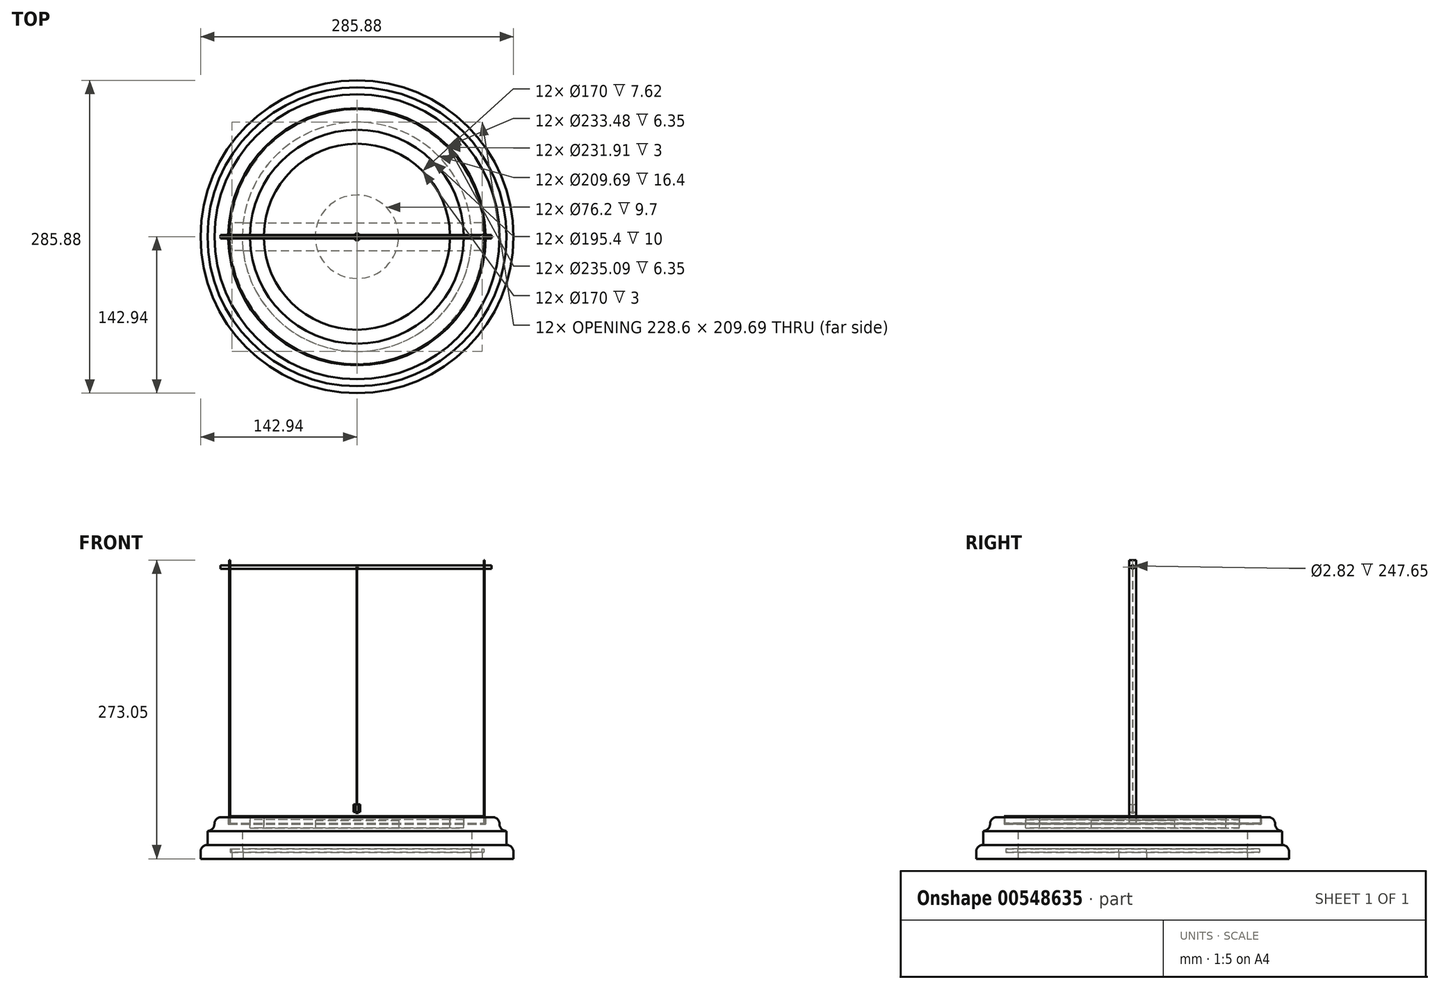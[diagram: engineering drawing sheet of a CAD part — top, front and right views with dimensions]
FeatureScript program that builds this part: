
annotation { "Feature Type Name" : "Feature", "Feature Type Description" : "" }
export const myFeature = defineFeature(function(context is Context, id is Id, definition is map)
    precondition{}
    {
        {
            var Q0;
            Q0=qCreatedBy(makeId("Front.planeOp"),FACE);
            var sketch = newSketch(context, id + "F0", { "sketchPlane" : qUnion([Q0])});
            skLineSegment(sketch, "E0", {"start": v(0, 38.1) * mm, "end": v(-85, 38.1) * mm});
            skLineSegment(sketch, "E1", {"start": v(-85, 38.1) * mm, "end": v(-85, 28.1) * mm});
            skLineSegment(sketch, "E2", {"start": v(-97.7, 28.1) * mm, "end": v(-97.7, 38.1) * mm});
            skLineSegment(sketch, "E3", {"start": v(-97.7, 38.1) * mm, "end": v(-116.75, 38.1) * mm});
            skLineSegment(sketch, "E4", {"start": v(-142.94, 0) * mm, "end": v(-104.84, 0) * mm});
            skLineSegment(sketch, "E5", {"start": v(-104.84, 25.4) * mm, "end": v(-104.84, 9) * mm});
            skLineSegment(sketch, "E6", {"start": v(-104.84, 9) * mm, "end": v(-115.96, 9) * mm});
            skLineSegment(sketch, "E7", {"start": v(-115.96, 9) * mm, "end": v(-115.96, 6) * mm});
            skLineSegment(sketch, "E8", {"start": v(-115.96, 6) * mm, "end": v(-104.84, 6) * mm});
            skLineSegment(sketch, "E9", {"start": v(-104.84, 6) * mm, "end": v(-104.84, 0) * mm});
            skLineSegment(sketch, "E10", {"start": v(-136.6, 12.7) * mm, "end": v(-136.6, 25.4) * mm});
            skArc(sketch, "E11", {"start": v(-136.6, 25.4) * mm, "mid": v(-132.1, 27.26) * mm, "end": v(-130.24, 31.75) * mm});
            skLineSegment(sketch, "E12", {"start": v(-117.54, 38.1) * mm, "end": v(-117.54, 31.75) * mm});
            skLineSegment(sketch, "E13", {"start": v(-117.54, 31.75) * mm, "end": v(-116.75, 31.75) * mm});
            skLineSegment(sketch, "E14", {"start": v(-116.75, 31.75) * mm, "end": v(-116.75, 38.1) * mm});
            skLineSegment(sketch, "E15", {"start": v(-97.7, 28.1) * mm, "end": v(-85, 28.1) * mm});
            skLineSegment(sketch, "E16", {"start": v(-117.54, 38.1) * mm, "end": v(-123.9, 38.1) * mm});
            skArc(sketch, "E17", {"start": v(-123.9, 38.1) * mm, "mid": v(-128.38, 36.24) * mm, "end": v(-130.24, 31.75) * mm});
            skLineSegment(sketch, "E18", {"start": v(-136.6, 31.75) * mm, "end": v(-130.24, 31.75) * mm, "construction": true});
            skLineSegment(sketch, "E19", {"start": v(-123.9, 31.75) * mm, "end": v(-130.24, 31.75) * mm, "construction": true});
            skLineSegment(sketch, "E20", {"start": v(-136.6, 31.75) * mm, "end": v(-136.6, 25.4) * mm, "construction": true});
            skLineSegment(sketch, "E21", {"start": v(-123.9, 38.1) * mm, "end": v(-123.9, 31.75) * mm, "construction": true});
            skArc(sketch, "E22", {"start": v(-136.6, 12.7) * mm, "mid": v(-141.08, 10.84) * mm, "end": v(-142.94, 6.35) * mm});
            skLineSegment(sketch, "E23", {"start": v(-136.6, 12.7) * mm, "end": v(-136.6, 6.35) * mm, "construction": true});
            skLineSegment(sketch, "E24", {"start": v(-136.6, 6.35) * mm, "end": v(-142.94, 6.35) * mm, "construction": true});
            skLineSegment(sketch, "E25", {"start": v(-142.94, 6.35) * mm, "end": v(-142.94, 0) * mm});
            skLineSegment(sketch, "E26", {"start": v(-104.84, 25.4) * mm, "end": v(-38.1, 25.4) * mm});
            skLineSegment(sketch, "E27", {"start": v(-38.1, 25.4) * mm, "end": v(-38.1, 35.1) * mm});
            skLineSegment(sketch, "E28", {"start": v(-38.1, 35.1) * mm, "end": v(0, 35.1) * mm});
            skLineSegment(sketch, "E29", {"start": v(0, 35.1) * mm, "end": v(0, 38.1) * mm});
            skSolve(sketch);
        }
        {
            var Q0;
            Q0=makeQuery(id+"F0.imprint","IMPRINT",FACE,{"disambiguationData":[TD([[makeQuery(id+"F0.imprint","IMPRINT",EDGE,{"derivedFrom":sQuery(id+"F0.wireOp",EDGE,"E0")}),1.0]])]});
            var Q1;
            Q1=sQuery(id+"F0.wireOp",EDGE,"E29");
            revolve(context, id + "F1", {"entities" : qUnion([Q0]), "axis" : qUnion([Q1]), "revolveType" : RevolveType.FULL});
        }
        {
            var Q0;
            Q0=makeQuery(id+"F1.opRevolve","SWEPT_FACE",FACE,{"disambiguationData":[OSD([sQuery(id+"F0.wireOp",EDGE,"E4")])]});
            var sketch = newSketch(context, id + "F2", { "sketchPlane" : qUnion([Q0])});
            skLineSegment(sketch, "E30.bottom", {"start": v(-114.3, 12.7) * mm, "end": v(114.3, 12.7) * mm});
            skLineSegment(sketch, "E30.top", {"start": v(-114.3, -12.7) * mm, "end": v(114.3, -12.7) * mm});
            skLineSegment(sketch, "E30.left", {"start": v(-114.3, 12.7) * mm, "end": v(-114.3, -12.7) * mm});
            skLineSegment(sketch, "E30.right", {"start": v(114.3, 12.7) * mm, "end": v(114.3, -12.7) * mm});
            skPoint(sketch, "E30.middle", {"position": v(0, 0) * mm});
            skSolve(sketch);
        }
        {
            var Q0;
            Q0 = qSketchRegion(id + "F2", true);
            var Q1;
            Q1=makeQuery(id+"F1.opRevolve","SWEPT_FACE",FACE,{"disambiguationData":[OSD([sQuery(id+"F0.wireOp",EDGE,"E6")])]});
            extrude(context, id + "F3", {"entities" : qUnion([Q0]), "operationType" : NewBodyOperationType.REMOVE, "endBound" : BoundingType.UP_TO_SURFACE, "oppositeDirection" : true, "depth" : 25.4 * mm, "endBoundEntityFace" : qUnion([Q1]), "offsetDistance" : 25.4 * mm});
        }
        {
            var Q0;
            Q0=makeQuery(id+"F1.opRevolve","SWEPT_FACE",FACE,{"disambiguationData":[OSD([sQuery(id+"F0.wireOp",EDGE,"E3")])]});
            var sketch = newSketch(context, id + "F4", { "sketchPlane" : qUnion([Q0])});
            skLineSegment(sketch, "E31.bottom", {"start": v(-116.62, 3.17) * mm, "end": v(-115.82, 3.17) * mm});
            skLineSegment(sketch, "E31.top", {"start": v(-116.62, -3.18) * mm, "end": v(-115.82, -3.18) * mm});
            skLineSegment(sketch, "E31.left", {"start": v(-116.62, 3.17) * mm, "end": v(-116.62, -3.17) * mm});
            skLineSegment(sketch, "E31.right", {"start": v(-115.82, 3.17) * mm, "end": v(-115.82, -3.18) * mm});
            skLineSegment(sketch, "E32", {"start": v(-115.82, 0) * mm, "end": v(0, 0) * mm, "construction": true});
            skLineSegment(sketch, "E33.bottom", {"start": v(115.82, 3.18) * mm, "end": v(116.62, 3.18) * mm});
            skLineSegment(sketch, "E33.top", {"start": v(115.82, -3.17) * mm, "end": v(116.62, -3.17) * mm});
            skLineSegment(sketch, "E33.left", {"start": v(115.82, 3.18) * mm, "end": v(115.82, -3.17) * mm});
            skLineSegment(sketch, "E33.right", {"start": v(116.62, 3.17) * mm, "end": v(116.62, -3.18) * mm});
            skLineSegment(sketch, "E34", {"start": v(115.82, 0) * mm, "end": v(0, 0) * mm, "construction": true});
            skSolve(sketch);
        }
        {
            var Q0;
            Q0=makeQuery(id+"F4.imprint","IMPRINT",FACE,{"disambiguationData":[TD([[makeQuery(id+"F4.imprint","IMPRINT",EDGE,{"derivedFrom":sQuery(id+"F4.wireOp",EDGE,"E31.bottom")}),-1.0]])]});
            var Q1;
            Q1=makeQuery(id+"F4.imprint","IMPRINT",FACE,{"disambiguationData":[TD([[makeQuery(id+"F4.imprint","IMPRINT",EDGE,{"derivedFrom":sQuery(id+"F4.wireOp",EDGE,"E33.bottom")}),-1.0]])]});
            extrude(context, id + "F5", {"entities" : qUnion([Q0, Q1]), "operationType" : NewBodyOperationType.REMOVE, "oppositeDirection" : true, "depth" : 6.35 * mm, "offsetDistance" : 25.4 * mm});
        }
        {
            var Q0;
            Q0=qCreatedBy(makeId("Front.planeOp"),FACE);
            var sketch = newSketch(context, id + "F6", { "sketchPlane" : qUnion([Q0])});
            skLineSegment(sketch, "E35", {"start": v(-85, 35.71) * mm, "end": v(-85, 28.1) * mm});
            skLineSegment(sketch, "E36", {"start": v(-85, 28.1) * mm, "end": v(-97.7, 28.1) * mm});
            skLineSegment(sketch, "E37", {"start": v(-97.7, 28.1) * mm, "end": v(-97.7, 35.71) * mm});
            skLineSegment(sketch, "E38", {"start": v(-97.7, 35.71) * mm, "end": v(-85, 35.71) * mm});
            skLineSegment(sketch, "E39", {"start": v(0, 35.71) * mm, "end": v(0, 28.1) * mm, "construction": true});
            skLineSegment(sketch, "E40", {"start": v(0, 28.1) * mm, "end": v(0, 0) * mm, "construction": true});
            skSolve(sketch);
        }
        {
            var Q0;
            Q0 = qSketchRegion(id + "F6", true);
            var Q1;
            Q1=sQuery(id+"F6.wireOp",EDGE,"E39");
            revolve(context, id + "F7", {"entities" : qUnion([Q0]), "axis" : qUnion([Q1]), "revolveType" : RevolveType.FULL});
        }
        {
            var Q0;
            Q0=qCreatedBy(makeId("Front.planeOp"),FACE);
            var sketch = newSketch(context, id + "F8", { "sketchPlane" : qUnion([Q0])});
            skLineSegment(sketch, "E41", {"start": v(0, 35.71) * mm, "end": v(0, 38.71) * mm});
            skLineSegment(sketch, "E42", {"start": v(0, 35.71) * mm, "end": v(0, 0) * mm, "construction": true});
            skLineSegment(sketch, "E43", {"start": v(-97.7, 38.71) * mm, "end": v(-85, 38.71) * mm});
            skLineSegment(sketch, "E44", {"start": v(-85, 38.71) * mm, "end": v(-85, 35.71) * mm});
            skLineSegment(sketch, "E45", {"start": v(-85, 35.71) * mm, "end": v(-97.7, 35.71) * mm});
            skLineSegment(sketch, "E46", {"start": v(-97.7, 35.71) * mm, "end": v(-97.7, 38.71) * mm});
            skLineSegment(sketch, "E47", {"start": v(-85, 35.71) * mm, "end": v(0, 35.71) * mm, "construction": true});
            skSolve(sketch);
        }
        {
            var Q0;
            Q0 = qSketchRegion(id + "F8", true);
            var Q1;
            Q1=sQuery(id+"F8.wireOp",EDGE,"E41");
            revolve(context, id + "F9", {"entities" : qUnion([Q0]), "axis" : qUnion([Q1]), "revolveType" : RevolveType.FULL});
        }
        {
            var Q0;
            Q0=qCreatedBy(makeId("Front.planeOp"),FACE);
            var sketch = newSketch(context, id + "F10", { "sketchPlane" : qUnion([Q0])});
            skLineSegment(sketch, "E48", {"start": v(0, 0) * mm, "end": v(0, 32.54) * mm, "construction": true});
            skLineSegment(sketch, "E49", {"start": v(0, 32.54) * mm, "end": v(-116.74, 32.54) * mm, "construction": true});
            skLineSegment(sketch, "E50", {"start": v(-116.74, 32.54) * mm, "end": v(-116.74, 38.9) * mm});
            skLineSegment(sketch, "E51", {"start": v(-116.74, 38.9) * mm, "end": v(-117.53, 38.9) * mm});
            skLineSegment(sketch, "E52", {"start": v(-117.53, 38.9) * mm, "end": v(-117.53, 32.54) * mm});
            skLineSegment(sketch, "E53", {"start": v(-117.53, 32.54) * mm, "end": v(-116.74, 32.54) * mm});
            skSolve(sketch);
        }
        {
            var Q0;
            Q0 = qSketchRegion(id + "F10", true);
            var Q1;
            Q1=sQuery(id+"F10.wireOp",EDGE,"E48");
            revolve(context, id + "F11", {"entities" : qUnion([Q0]), "axis" : qUnion([Q1]), "revolveType" : RevolveType.FULL});
        }
        {
            var Q0;
            Q0=makeQuery(id+"F1.opRevolve","SWEPT_FACE",FACE,{"disambiguationData":[OSD([sQuery(id+"F0.wireOp",EDGE,"E6")])]});
            var sketch = newSketch(context, id + "F12", { "sketchPlane" : qUnion([Q0])});
            skArc(sketch, "E54.0", {"start": v(104.07, 12.7) * mm, "mid": v(0, 104.84) * mm, "end": v(-104.07, 12.7) * mm});
            skArc(sketch, "E55.0", {"start": v(-104.07, -12.7) * mm, "mid": v(0, -104.84) * mm, "end": v(104.07, -12.7) * mm});
            skLineSegment(sketch, "E56.0", {"start": v(104.07, 12.7) * mm, "end": v(114.3, 12.7) * mm});
            skLineSegment(sketch, "E56.1", {"start": v(114.3, 12.7) * mm, "end": v(114.3, -12.7) * mm});
            skLineSegment(sketch, "E56.2", {"start": v(104.07, -12.7) * mm, "end": v(114.3, -12.7) * mm});
            skLineSegment(sketch, "E57.0", {"start": v(-114.3, 12.7) * mm, "end": v(-104.07, 12.7) * mm});
            skLineSegment(sketch, "E57.1", {"start": v(-114.3, 12.7) * mm, "end": v(-114.3, -12.7) * mm});
            skLineSegment(sketch, "E57.2", {"start": v(-114.3, -12.7) * mm, "end": v(-104.07, -12.7) * mm});
            skSolve(sketch);
        }
        {
            var Q0;
            {var subQ0=sQuery(id+"F12.wireOp",EDGE,"E56.0");Q0=makeQuery(id+"F12.imprint","IMPRINT",FACE,{"disambiguationData":[TD([[makeQuery(id+"F12.imprint","IMPRINT",EDGE,{"derivedFrom":subQ0}),-1.0]])]});}
            var Q1;
            {var subQ0=sQuery(id+"F12.wireOp",EDGE,"E57.0");Q1=makeQuery(id+"F12.imprint","IMPRINT",FACE,{"disambiguationData":[TD([[makeQuery(id+"F12.imprint","IMPRINT",EDGE,{"derivedFrom":subQ0}),-1.0]])]});}
            var Q2;
            {var subQ0=sQuery(id+"F12.wireOp",EDGE,"E54.0");Q2=makeQuery(id+"F12.imprint","IMPRINT",FACE,{"disambiguationData":[TD([[makeQuery(id+"F12.imprint","IMPRINT",EDGE,{"derivedFrom":subQ0}),1.0]])]});}
            extrude(context, id + "F13", {"entities" : qUnion([Q0, Q1, Q2]), "depth" : 3 * mm, "offsetDistance" : 25.4 * mm});
        }
        {
            var Q0;
            Q0=makeQuery(id+"F5.boolean.opBoolean","COPY",FACE,{"derivedFrom":makeQuery(id+"F5.opExtrude","CAP_FACE",FACE,{"disambiguationData":[OSD([sQuery(id+"F4.wireOp",EDGE,"E31.bottom"),sQuery(id+"F4.wireOp",EDGE,"E31.top"),sQuery(id+"F4.wireOp",EDGE,"E31.left"),sQuery(id+"F4.wireOp",EDGE,"E31.right")])],"isStart":false})});
            var sketch = newSketch(context, id + "F14", { "sketchPlane" : qUnion([Q0])});
            skLineSegment(sketch, "E58.bottom", {"start": v(-115.82, 3.17) * mm, "end": v(-116.62, 3.17) * mm});
            skLineSegment(sketch, "E58.top", {"start": v(-115.82, -3.17) * mm, "end": v(-116.62, -3.17) * mm});
            skLineSegment(sketch, "E58.left", {"start": v(-115.82, 3.17) * mm, "end": v(-115.82, -3.17) * mm});
            skLineSegment(sketch, "E58.right", {"start": v(-116.62, 3.17) * mm, "end": v(-116.62, -3.17) * mm});
            skLineSegment(sketch, "E59.bottom", {"start": v(115.82, 3.18) * mm, "end": v(116.61, 3.18) * mm});
            skLineSegment(sketch, "E59.top", {"start": v(115.82, -3.17) * mm, "end": v(116.61, -3.17) * mm});
            skLineSegment(sketch, "E59.left", {"start": v(115.82, 3.18) * mm, "end": v(115.82, -3.17) * mm});
            skLineSegment(sketch, "E59.right", {"start": v(116.61, 3.18) * mm, "end": v(116.61, -3.17) * mm});
            skSolve(sketch);
        }
        {
            var Q0;
            Q0=makeQuery(id+"F14.imprint","IMPRINT",FACE,{"disambiguationData":[TD([[makeQuery(id+"F14.imprint","IMPRINT",EDGE,{"derivedFrom":sQuery(id+"F14.wireOp",EDGE,"E59.bottom")}),-1.0]])]});
            var Q1;
            Q1=makeQuery(id+"F14.imprint","IMPRINT",FACE,{"disambiguationData":[TD([[makeQuery(id+"F14.imprint","IMPRINT",EDGE,{"derivedFrom":sQuery(id+"F14.wireOp",EDGE,"E58.bottom")}),-1.0]])]});
            extrude(context, id + "F15", {"entities" : qUnion([Q0, Q1]), "depth" : 241.3 * mm, "offsetDistance" : 25.4 * mm});
        }
        {
            var Q0;
            Q0=makeQuery(id+"F15.opExtrude","SWEPT_FACE",FACE,{"disambiguationData":[OSD([sQuery(id+"F14.wireOp",EDGE,"E59.right")])]});
            var sketch = newSketch(context, id + "F16", { "sketchPlane" : qUnion([Q0])});
            skCircle(sketch, "E60", {"center": v(0, 266.7) * mm, "radius": 1.59 * mm});
            skLineSegment(sketch, "E61", {"start": v(0, 266.7) * mm, "end": v(0, 273.05) * mm, "construction": true});
            skSolve(sketch);
        }
        {
            var Q0;
            Q0 = qSketchRegion(id + "F16", true);
            extrude(context, id + "F17", {"entities" : qUnion([Q0]), "operationType" : NewBodyOperationType.REMOVE, "endBound" : BoundingType.THROUGH_ALL, "oppositeDirection" : true, "depth" : 25.4 * mm, "offsetDistance" : 25.4 * mm});
        }
        {
            var Q0;
            Q0=makeQuery(id+"F15.opExtrude","SWEPT_FACE",FACE,{"disambiguationData":[OSD([sQuery(id+"F14.wireOp",EDGE,"E59.right")])]});
            var sketch = newSketch(context, id + "F18", { "sketchPlane" : qUnion([Q0])});
            skCircle(sketch, "E62", {"center": v(0, 266.7) * mm, "radius": 1.59 * mm});
            skCircle(sketch, "E63", {"center": v(0, 266.7) * mm, "radius": 1.4 * mm});
            skSolve(sketch);
        }
        {
            var Q0;
            Q0=makeQuery(id+"F18.imprint","IMPRINT",FACE,{"disambiguationData":[TD([[makeQuery(id+"F18.imprint","IMPRINT",EDGE,{"derivedFrom":sQuery(id+"F18.wireOp",EDGE,"E62")}),1.0]])]});
            var Q1;
            Q1=makeQuery(id+"F15.opExtrude","SWEPT_FACE",FACE,{"disambiguationData":[OSD([sQuery(id+"F14.wireOp",EDGE,"E58.right")])]});
            extrude(context, id + "F19", {"entities" : qUnion([Q0]), "oppositeDirection" : true, "depth" : 241.3 * mm, "endBoundEntityFace" : qUnion([Q1]), "offsetDistance" : 25.4 * mm, "hasSecondDirection" : true, "secondDirectionOppositeDirection" : false, "secondDirectionDepth" : 6.35 * mm});
        }
        {
            var Q0;
            Q0=makeQuery(id+"F1.opRevolve","SWEPT_FACE",FACE,{"disambiguationData":[OSD([sQuery(id+"F0.wireOp",EDGE,"E0")])]});
            var sketch = newSketch(context, id + "F20", { "sketchPlane" : qUnion([Q0])});
            skCircle(sketch, "E64", {"center": v(0, 0) * mm, "radius": 0.4 * mm});
            skSolve(sketch);
        }
        {
            var Q0;
            Q0 = qSketchRegion(id + "F20", true);
            extrude(context, id + "F21", {"entities" : qUnion([Q0]), "operationType" : NewBodyOperationType.REMOVE, "depth" : 228.6 * mm, "offsetDistance" : 25.4 * mm});
        }
        {
            var Q0;
            Q0=qCreatedBy(makeId("Front.planeOp"),FACE);
            var sketch = newSketch(context, id + "F22", { "sketchPlane" : qUnion([Q0])});
            skLineSegment(sketch, "E65", {"start": v(0, 266.7) * mm, "end": v(-1.23, 266.7) * mm});
            skLineSegment(sketch, "E66", {"start": v(-1.23, 266.7) * mm, "end": v(-1.23, 265.47) * mm});
            skLineSegment(sketch, "E67", {"start": v(-1.23, 265.47) * mm, "end": v(-0.1, 265.47) * mm});
            skLineSegment(sketch, "E68", {"start": v(-0.1, 265.47) * mm, "end": v(-0.1, 265.11) * mm});
            skLineSegment(sketch, "E69", {"start": v(-0.1, 265.11) * mm, "end": v(-0.1, 42.86) * mm});
            skLineSegment(sketch, "E70.0", {"start": v(123.9, 38.1) * mm, "end": v(-123.9, 38.1) * mm});
            skLineSegment(sketch, "E71", {"start": v(-0.1, 42.86) * mm, "end": v(-1.23, 42.86) * mm});
            skLineSegment(sketch, "E72", {"start": v(-1.23, 42.86) * mm, "end": v(-1.23, 41.63) * mm});
            skLineSegment(sketch, "E73", {"start": v(-1.23, 41.63) * mm, "end": v(0, 41.63) * mm});
            skLineSegment(sketch, "E74", {"start": v(0, 41.63) * mm, "end": v(0, 266.7) * mm});
            skSolve(sketch);
        }
        {
            var Q0;
            Q0 = qSketchRegion(id + "F22", true);
            var Q1;
            Q1=sQuery(id+"F22.wireOp",EDGE,"E74");
            revolve(context, id + "F23", {"entities" : qUnion([Q0]), "axis" : qUnion([Q1]), "revolveType" : RevolveType.FULL});
        }
        {
            var Q0;
            Q0=makeQuery(id+"F23.opRevolve","SWEPT_FACE",FACE,{"disambiguationData":[OSD([sQuery(id+"F22.wireOp",EDGE,"E71")])]});
            var sketch = newSketch(context, id + "F24", { "sketchPlane" : qUnion([Q0])});
            skLineSegment(sketch, "E75", {"start": v(-1.65, 3) * mm, "end": v(1.65, 3) * mm});
            skLineSegment(sketch, "E76", {"start": v(1.65, 3) * mm, "end": v(3, 0) * mm});
            skLineSegment(sketch, "E77", {"start": v(3, 0) * mm, "end": v(1.65, -3) * mm});
            skLineSegment(sketch, "E78", {"start": v(1.65, -3) * mm, "end": v(-1.65, -3) * mm});
            skLineSegment(sketch, "E79", {"start": v(-1.65, -3) * mm, "end": v(-3, 0) * mm});
            skLineSegment(sketch, "E80", {"start": v(-3, 0) * mm, "end": v(-1.65, 3) * mm});
            skLineSegment(sketch, "E81", {"start": v(-1.65, 3) * mm, "end": v(-1.65, -3) * mm, "construction": true});
            skLineSegment(sketch, "E82", {"start": v(1.65, 3) * mm, "end": v(1.65, -3) * mm, "construction": true});
            skLineSegment(sketch, "E83", {"start": v(-3, 0) * mm, "end": v(3, 0) * mm, "construction": true});
            skCircle(sketch, "E84", {"center": v(0, 0) * mm, "radius": 0.5 * mm});
            skLineSegment(sketch, "E85", {"start": v(0, 3) * mm, "end": v(0, -3) * mm, "construction": true});
            skSolve(sketch);
        }
        {
            var Q0;
            Q0=makeQuery(id+"F24.imprint","IMPRINT",FACE,{"disambiguationData":[TD([[makeQuery(id+"F24.imprint","IMPRINT",EDGE,{"derivedFrom":sQuery(id+"F24.wireOp",EDGE,"E75")}),-1.0]])]});
            var Q1;
            Q1=makeQuery(id+"F24.imprint","IMPRINT",FACE,{"disambiguationData":[TD([[makeQuery(id+"F24.imprint","IMPRINT",EDGE,{"derivedFrom":sQuery(id+"F24.wireOp",EDGE,"E84")}),-1.0]])]});
            extrude(context, id + "F25", {"entities" : qUnion([Q0, Q1]), "depth" : 7 * mm, "offsetDistance" : 25.4 * mm});
        }
    });
